# Revit family: Furniture_Office-Chairs_Flokk_Giroflex-353_Swivel-Armrests
name_source: partatom
category: Furniture
units: mm (PartAtom-declared; Revit-internal decimal feet)

## family parameters
Always vertical = Yes
Cut with Voids When Loaded = No
OmniClass Number = 23.40.20.14.14.11
OmniClass Title = Chairs
Room Calculation Point = No
Shared = No
Work Plane-Based = No

## types (3) — shared parameters
AssetType = Movable
BIMObjectName = Furniture_Office-Chairs_Flokk_Giroflex-353_Swivel-Armrests
Brand = Flokk
Category = Giroflex
Color = Various
Description = The giroflex 353 swivel chair is the chair for the personal touch. With its innovative mechanism it automatically adapts to its occupants.
DurationUnit = Year
HighestSeatingHeight = 500 mm  [stored 1.64042 ft]
IfcExportAs = IfcFurnishingElementType
IfcExportType = CHAIR
LowestSeatingHeight = 500 mm  [stored 1.64042 ft]
MainColor = Various
Manufacturer = Flokk
ManufacturerName = Flokk
ManufacturerURL = https://www.flokk.com
Material = Plastic, Metal and Textile
ModelNumber = 353-4029
NBSDescription = Stacking chairs
NBSReference = 45-35-20/355
Name = Giroflex-353_Swivel-Armrests
NominalDepth = 681 mm
NominalHeight = 1085 mm
NominalLength = 698 mm
OfficeChairQuaternaryMaterial = Black RAL 9005
ProductDatasheet = https://flokkplatformprod.blob.core.windows.net
ProductInformation = The giroflex 353 swivel chair is the chair for the personal touch. With its innovative mechanism it automatically adapts to its occupants.
SeatingHeight = 500 mm  [stored 1.64042 ft]
Shape = Sculptured
Size = 700x680x970 mm
URL = https://store.flokk.com
Uniclass2 = Pr_40_50_12_51
Uniclass2015Description = Meeting room chairs
Uniclass2015Reference = Pr_40_50_12_51
Version = 1
VersionDate = 05/01/2023
WarrantyDurationUnit = Year
zero-valued in all types: Cost, Default Elevation

## per-type parameters (varying)
| type | ChairType |
| Giroflex 353 swivel, armrests fixed | giroflex_353_swivel_arm_fixed |
| Giroflex 353 swivel, armrests 2D | giroflex_353_swivel_arm_2d |
| Giroflex 353 swivel, armrests 4D | giroflex_353_swivel_arm_4d |

note: column(s) folded — value = type name in every type: Model

note: [stored X ft] marks values corroborated as IEEE doubles in the binary element streams (Revit-internal decimal feet)

## geometry (parser evidence)
native form markers: Sweep x12
no freeform markers — native parametric forms only
